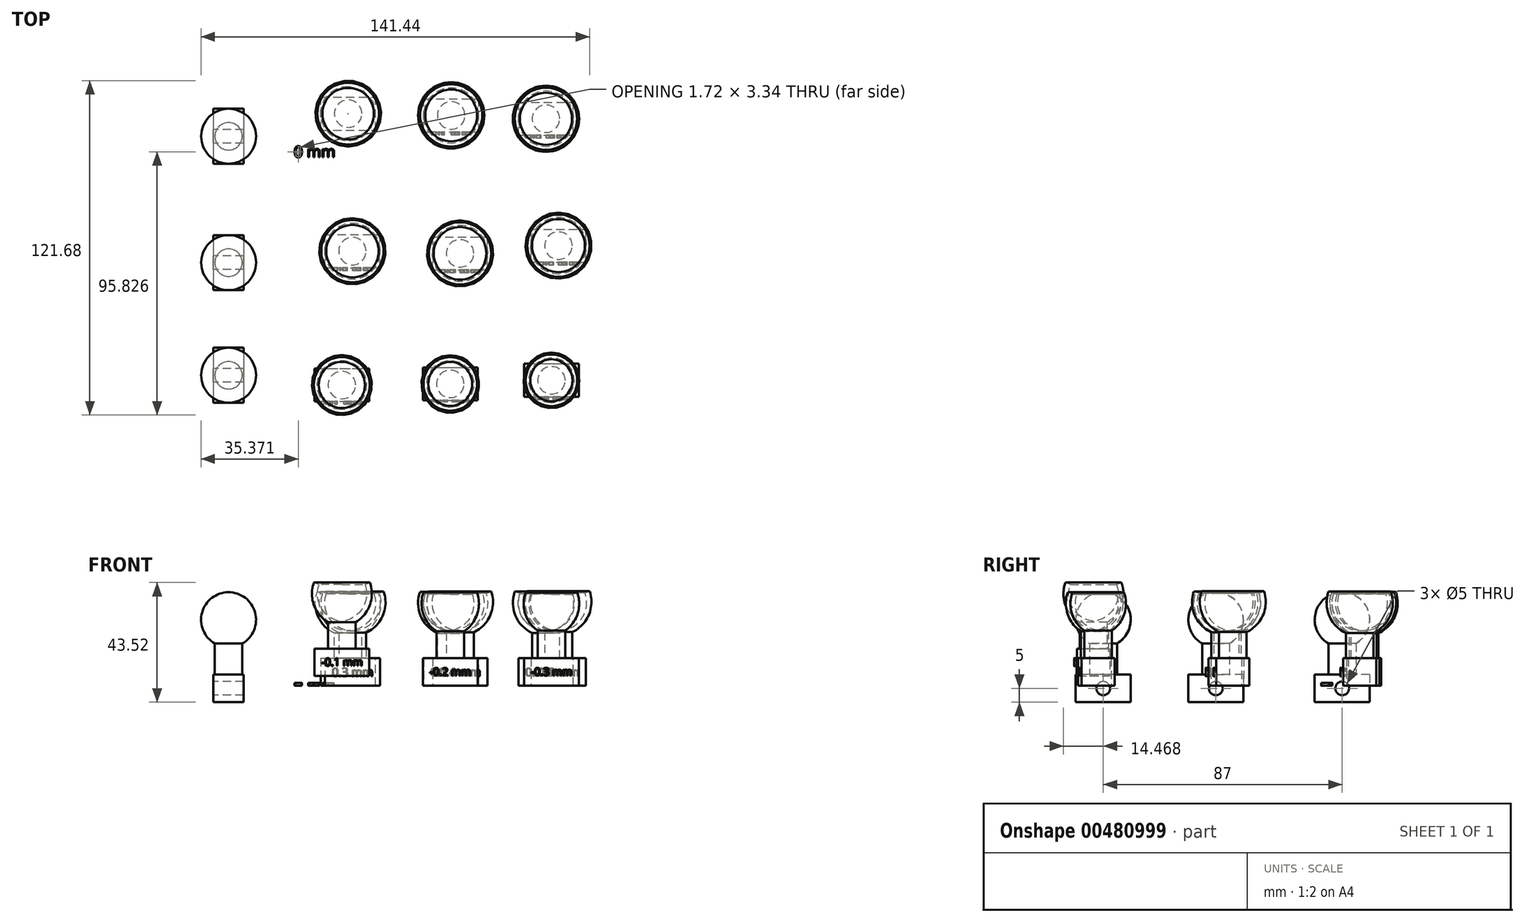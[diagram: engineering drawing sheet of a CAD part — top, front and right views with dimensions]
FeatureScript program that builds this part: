
annotation { "Feature Type Name" : "Feature", "Feature Type Description" : "" }
export const myFeature = defineFeature(function(context is Context, id is Id, definition is map)
    precondition{}
    {
        {
            var Q0;
            Q0=qCreatedBy(makeId("Top.planeOp"),FACE);
            var sketch = newSketch(context, id + "F0", { "sketchPlane" : qUnion([Q0])});
            skLineSegment(sketch, "E0", {"start": v(-54.8, 58.63) * mm, "end": v(-54.8, 38.63) * mm});
            skLineSegment(sketch, "E1", {"start": v(-54.8, 58.63) * mm, "end": v(-64.8, 58.63) * mm});
            skLineSegment(sketch, "E2", {"start": v(-64.8, 58.63) * mm, "end": v(-64.8, 38.63) * mm});
            skLineSegment(sketch, "E3", {"start": v(-64.8, 38.63) * mm, "end": v(-54.8, 38.63) * mm});
            skLineSegment(sketch, "E4", {"start": v(-54.8, 53.63) * mm, "end": v(-43.46, 53.63) * mm});
            skLineSegment(sketch, "E5", {"start": v(-44.8, 48.63) * mm, "end": v(-24.8, 48.63) * mm});
            skArc(sketch, "E6", {"start": v(-24.8, 48.63) * mm, "mid": v(-34.8, 58.63) * mm, "end": v(-44.8, 48.63) * mm});
            skLineSegment(sketch, "E7", {"start": v(-44.8, 48.63) * mm, "end": v(-54.8, 48.63) * mm});
            skSolve(sketch);
        }
        {
            var Q0;
            {var subQ0=sQuery(id+"F0.wireOp",EDGE,"E4");Q0=makeQuery(id+"F0.imprint","IMPRINT",FACE,{"disambiguationData":[TD([[makeQuery(id+"F0.imprint","IMPRINT",EDGE,{"derivedFrom":subQ0}),-1.0]])]});}
            var Q1;
            {var subQ0=sQuery(id+"F0.wireOp",EDGE,"E5");Q1=makeQuery(id+"F0.imprint","IMPRINT",FACE,{"disambiguationData":[TD([[makeQuery(id+"F0.imprint","IMPRINT",EDGE,{"derivedFrom":subQ0}),1.0]])]});}
            var Q2;
            Q2=sQuery(id+"F0.wireOp",EDGE,"E5");
            revolve(context, id + "F1", {"entities" : qUnion([Q0, Q1]), "axis" : qUnion([Q2]), "revolveType" : RevolveType.FULL});
        }
        {
            var Q0;
            {var subQ0=sQuery(id+"F0.wireOp",EDGE,"E1");Q0=makeQuery(id+"F0.imprint","IMPRINT",FACE,{"disambiguationData":[TD([[makeQuery(id+"F0.imprint","IMPRINT",EDGE,{"derivedFrom":subQ0}),1.0]])]});}
            extrude(context, id + "F2", {"entities" : qUnion([Q0]), "operationType" : NewBodyOperationType.ADD, "endBound" : BoundingType.SYMMETRIC, "depth" : 11 * mm});
        }
        {
            var Q0;
            Q0=makeQuery(id+"F1.opRevolve","SWEPT_BODY",BODY,{"disambiguationData":[OSD([sQuery(id+"F0.wireOp",EDGE,"E0"),sQuery(id+"F0.wireOp",EDGE,"E4"),sQuery(id+"F0.wireOp",EDGE,"E5"),sQuery(id+"F0.wireOp",EDGE,"E6"),sQuery(id+"F0.wireOp",EDGE,"E7")])]});
            var Q1;
            Q1=sQuery(id+"F0.wireOp",EDGE,"E2");
            transform(context, id + "F3", {"entities" : qUnion([Q0]), "transformType" : TransformType.ROTATION, "transformAxis" : qUnion([Q1]), "angle" : 90 * degree, "makeCopy" : false});
        }
        {
            var Q0;
            Q0=makeQuery(id+"F1.opRevolve","SWEPT_BODY",BODY,{"disambiguationData":[OSD([sQuery(id+"F0.wireOp",EDGE,"E0"),sQuery(id+"F0.wireOp",EDGE,"E4"),sQuery(id+"F0.wireOp",EDGE,"E5"),sQuery(id+"F0.wireOp",EDGE,"E6"),sQuery(id+"F0.wireOp",EDGE,"E7")])]});
            var Q1;
            Q1=makeQuery(id+"F2.opExtrude","CAP_EDGE",EDGE,{"disambiguationData":[OSD([sQuery(id+"F0.wireOp",EDGE,"E0")])],"isStart":false});
            transform(context, id + "F4", {"entities" : qUnion([Q0]), "transformType" : TransformType.TRANSLATION_ENTITY, "oppositeDirectionEntity" : false, "transformLine" : qUnion([Q1]), "makeCopy" : true});
        }
        {
            var Q0;
            Q0=makeQuery(id+"F4.opPattern","COPY",BODY,{"derivedFrom":makeQuery(id+"F1.opRevolve","SWEPT_BODY",BODY,{"disambiguationData":[OSD([sQuery(id+"F0.wireOp",EDGE,"E0"),sQuery(id+"F0.wireOp",EDGE,"E4"),sQuery(id+"F0.wireOp",EDGE,"E5"),sQuery(id+"F0.wireOp",EDGE,"E6"),sQuery(id+"F0.wireOp",EDGE,"E7")])]}),"instanceName":"1"});
            var Q1;
            Q1=makeQuery(id+"F4.opPattern","COPY",EDGE,{"derivedFrom":makeQuery(id+"F2.opExtrude","CAP_EDGE",EDGE,{"disambiguationData":[OSD([sQuery(id+"F0.wireOp",EDGE,"E2")])],"isStart":false}),"instanceName":"1"});
            transform(context, id + "F5", {"entities" : qUnion([Q0]), "transformType" : TransformType.TRANSLATION_ENTITY, "oppositeDirectionEntity" : false, "transformLine" : qUnion([Q1]), "makeCopy" : false});
        }
        {
            var Q0;
            Q0=makeQuery(id+"F4.opPattern","COPY",BODY,{"derivedFrom":makeQuery(id+"F1.opRevolve","SWEPT_BODY",BODY,{"disambiguationData":[OSD([sQuery(id+"F0.wireOp",EDGE,"E0"),sQuery(id+"F0.wireOp",EDGE,"E4"),sQuery(id+"F0.wireOp",EDGE,"E5"),sQuery(id+"F0.wireOp",EDGE,"E6"),sQuery(id+"F0.wireOp",EDGE,"E7")])]}),"instanceName":"1"});
            var Q1;
            Q1=makeQuery(id+"F4.opPattern","COPY",EDGE,{"derivedFrom":makeQuery(id+"F2.opExtrude","CAP_EDGE",EDGE,{"disambiguationData":[OSD([sQuery(id+"F0.wireOp",EDGE,"E2")])],"isStart":false}),"instanceName":"1"});
            transform(context, id + "F6", {"entities" : qUnion([Q0]), "transformType" : TransformType.TRANSLATION_DISTANCE, "transformDirection" : qUnion([Q1]), "distance" : 40 * mm, "makeCopy" : true});
        }
        {
            var Q0;
            Q0=qCreatedBy(makeId("Top.planeOp"),FACE);
            var sketch = newSketch(context, id + "F7", { "sketchPlane" : qUnion([Q0])});
            skLineSegment(sketch, "E8", {"start": v(-31.27, 60.87) * mm, "end": v(-11.27, 60.87) * mm});
            skLineSegment(sketch, "E9", {"start": v(-31.27, 60.87) * mm, "end": v(-31.27, 50.87) * mm});
            skLineSegment(sketch, "E10", {"start": v(-31.27, 50.87) * mm, "end": v(-11.27, 50.87) * mm});
            skLineSegment(sketch, "E11", {"start": v(-11.27, 50.87) * mm, "end": v(-11.27, 60.87) * mm});
            skLineSegment(sketch, "E12", {"start": v(-26.27, 60.87) * mm, "end": v(-26.27, 72.22) * mm});
            skLineSegment(sketch, "E13", {"start": v(-21.27, 70.87) * mm, "end": v(-21.27, 90.87) * mm});
            skArc(sketch, "E14", {"start": v(-21.27, 90.87) * mm, "mid": v(-31.24, 80.87) * mm, "end": v(-21.27, 70.87) * mm});
            skLineSegment(sketch, "E15", {"start": v(-21.27, 70.87) * mm, "end": v(-21.27, 60.87) * mm});
            skArc(sketch, "E16", {"start": v(-21.27, 92.87) * mm, "mid": v(-33.24, 80.87) * mm, "end": v(-21.27, 68.87) * mm});
            skLineSegment(sketch, "E17", {"start": v(-21.27, 90.87) * mm, "end": v(-21.27, 92.87) * mm});
            skLineSegment(sketch, "E18", {"start": v(-21.24, 80.87) * mm, "end": v(-32.51, 84.97) * mm});
            skSolve(sketch);
        }
        {
            var Q0;
            {var subQ5=sQuery(id+"F7.wireOp",EDGE,"vTw5014h-nTbv-hpdb-avoR-3ejkp2Sw56j0");Q0=makeQuery(id+"F7.imprint","IMPRINT",FACE,{"disambiguationData":[TD([[makeQuery(id+"F7.imprint","IMPRINT",EDGE,{"derivedFrom":subQ5}),1.0]])]});}
            var Q1;
            {var subQ0=sQuery(id+"F7.wireOp",EDGE,"E14");var subQ1=sQuery(id+"F7.wireOp",EDGE,"E12");var subQ2=makeQuery(id+"F7.imprint","INTERSECT",VERTEX,{"derivedFrom":[subQ1,subQ0]});Q1=makeQuery(id+"F7.imprint","IMPRINT",FACE,{"disambiguationData":[TD([[makeQuery(id+"F7.imprint","IMPRINT",EDGE,{"disambiguationData":[TD([[subQ2,1.0]])],"derivedFrom":subQ1}),-1.0]])]});}
            var Q2;
            {var subQ0=sQuery(id+"F7.wireOp",EDGE,"E12");var subQ1=sQuery(id+"F7.wireOp",EDGE,"E8");var subQ2=makeQuery(id+"F7.imprint","INTERSECT",VERTEX,{"derivedFrom":[subQ1,subQ0]});Q2=makeQuery(id+"F7.imprint","IMPRINT",FACE,{"disambiguationData":[TD([[makeQuery(id+"F7.imprint","IMPRINT",EDGE,{"disambiguationData":[TD([[subQ2,-1.0]])],"derivedFrom":subQ1}),1.0]])]});}
            var Q3;
            {var subQ0=sQuery(id+"F7.wireOp",EDGE,"E14");var subQ1=sQuery(id+"F7.wireOp",EDGE,"E12");var subQ2=makeQuery(id+"F7.imprint","INTERSECT",VERTEX,{"derivedFrom":[subQ1,subQ0]});Q3=makeQuery(id+"F7.imprint","IMPRINT",FACE,{"disambiguationData":[TD([[makeQuery(id+"F7.imprint","IMPRINT",EDGE,{"disambiguationData":[TD([[subQ2,1.0]])],"derivedFrom":subQ1}),1.0]])]});}
            var Q4;
            Q4=sQuery(id+"F7.wireOp",EDGE,"E15");
            revolve(context, id + "F8", {"entities" : qUnion([Q0, Q1, Q2, Q3]), "axis" : qUnion([Q4]), "revolveType" : RevolveType.FULL});
        }
        {
            var Q0;
            {var subQ0=sQuery(id+"F7.wireOp",EDGE,"E9");Q0=makeQuery(id+"F7.imprint","IMPRINT",FACE,{"disambiguationData":[TD([[makeQuery(id+"F7.imprint","IMPRINT",EDGE,{"derivedFrom":subQ0}),1.0]])]});}
            extrude(context, id + "F9", {"entities" : qUnion([Q0]), "operationType" : NewBodyOperationType.ADD, "endBound" : BoundingType.SYMMETRIC, "depth" : 12 * mm});
        }
        {
            var Q0;
            Q0=makeQuery(id+"F9.opExtrude","CAP_FACE",FACE,{"disambiguationData":[OSD([sQuery(id+"F7.wireOp",EDGE,"E8"),sQuery(id+"F7.wireOp",EDGE,"E9"),sQuery(id+"F7.wireOp",EDGE,"E10"),sQuery(id+"F7.wireOp",EDGE,"E11")])],"isStart":false});
            var sketch = newSketch(context, id + "F10", { "sketchPlane" : qUnion([Q0])});
            skText(sketch, "E19", { "text": "0 mm", "fontName": "OpenSans-Regular.ttf"});
            const initialGuessF10  = {"E19": [-0.04103, 0.04098, 1, 0, 0.00404]};
            skSetInitialGuess(sketch, initialGuessF10);
            skSolve(sketch);
        }
        {
            var Q0;
            Q0 = qSketchRegion(id + "F10", true);
            extrude(context, id + "F11", {"entities" : qUnion([Q0]), "operationType" : NewBodyOperationType.ADD, "depth" : 1 * mm});
        }
        {
            var Q0;
            Q0=qCreatedBy(makeId("Top.planeOp"),FACE);
            var sketch = newSketch(context, id + "F12", { "sketchPlane" : qUnion([Q0])});
            skLineSegment(sketch, "E20", {"start": v(6.24, 60.21) * mm, "end": v(26.24, 60.21) * mm});
            skLineSegment(sketch, "E21", {"start": v(6.24, 60.21) * mm, "end": v(6.24, 50.21) * mm});
            skLineSegment(sketch, "E22", {"start": v(6.24, 50.21) * mm, "end": v(26.24, 50.21) * mm});
            skLineSegment(sketch, "E23", {"start": v(26.24, 50.21) * mm, "end": v(26.24, 60.21) * mm});
            skLineSegment(sketch, "E24", {"start": v(11.24, 60.21) * mm, "end": v(11.24, 71.54) * mm});
            skLineSegment(sketch, "E25", {"start": v(16.24, 70.21) * mm, "end": v(16.24, 90.31) * mm});
            skArc(sketch, "E26", {"start": v(16.24, 90.31) * mm, "mid": v(6.19, 80.26) * mm, "end": v(16.24, 70.21) * mm});
            skLineSegment(sketch, "E27", {"start": v(16.24, 70.21) * mm, "end": v(16.24, 60.21) * mm});
            skArc(sketch, "E28", {"start": v(16.24, 92.31) * mm, "mid": v(4.19, 80.26) * mm, "end": v(16.24, 68.21) * mm});
            skLineSegment(sketch, "E29", {"start": v(16.24, 90.31) * mm, "end": v(16.24, 92.31) * mm});
            skLineSegment(sketch, "E30", {"start": v(16.24, 80.26) * mm, "end": v(4.91, 84.38) * mm});
            skSolve(sketch);
        }
        {
            var Q0;
            {var subQ0=sQuery(id+"F12.wireOp",EDGE,"E26");var subQ1=sQuery(id+"F12.wireOp",EDGE,"E24");var subQ2=makeQuery(id+"F12.imprint","INTERSECT",VERTEX,{"derivedFrom":[subQ1,subQ0]});Q0=makeQuery(id+"F12.imprint","IMPRINT",FACE,{"disambiguationData":[TD([[makeQuery(id+"F12.imprint","IMPRINT",EDGE,{"disambiguationData":[TD([[subQ2,1.0]])],"derivedFrom":subQ1}),1.0]])]});}
            var Q1;
            {var subQ0=sQuery(id+"F12.wireOp",EDGE,"E26");var subQ1=sQuery(id+"F12.wireOp",EDGE,"E24");var subQ2=makeQuery(id+"F12.imprint","INTERSECT",VERTEX,{"derivedFrom":[subQ1,subQ0]});Q1=makeQuery(id+"F12.imprint","IMPRINT",FACE,{"disambiguationData":[TD([[makeQuery(id+"F12.imprint","IMPRINT",EDGE,{"disambiguationData":[TD([[subQ2,1.0]])],"derivedFrom":subQ1}),-1.0]])]});}
            var Q2;
            {var subQ0=sQuery(id+"F12.wireOp",EDGE,"E24");var subQ1=sQuery(id+"F12.wireOp",EDGE,"E20");var subQ2=makeQuery(id+"F12.imprint","INTERSECT",VERTEX,{"derivedFrom":[subQ1,subQ0]});Q2=makeQuery(id+"F12.imprint","IMPRINT",FACE,{"disambiguationData":[TD([[makeQuery(id+"F12.imprint","IMPRINT",EDGE,{"disambiguationData":[TD([[subQ2,-1.0]])],"derivedFrom":subQ1}),1.0]])]});}
            var Q3;
            Q3=sQuery(id+"F12.wireOp",EDGE,"E27");
            revolve(context, id + "F13", {"entities" : qUnion([Q0, Q1, Q2]), "axis" : qUnion([Q3]), "revolveType" : RevolveType.FULL});
        }
        {
            var Q0;
            {var subQ0=sQuery(id+"F12.wireOp",EDGE,"E21");Q0=makeQuery(id+"F12.imprint","IMPRINT",FACE,{"disambiguationData":[TD([[makeQuery(id+"F12.imprint","IMPRINT",EDGE,{"derivedFrom":subQ0}),1.0]])]});}
            extrude(context, id + "F14", {"entities" : qUnion([Q0]), "operationType" : NewBodyOperationType.ADD, "endBound" : BoundingType.SYMMETRIC, "depth" : 12 * mm});
        }
        {
            var Q0;
            Q0=makeQuery(id+"F14.opExtrude","CAP_FACE",FACE,{"disambiguationData":[OSD([sQuery(id+"F12.wireOp",EDGE,"E20"),sQuery(id+"F12.wireOp",EDGE,"E21"),sQuery(id+"F12.wireOp",EDGE,"E22"),sQuery(id+"F12.wireOp",EDGE,"E23")])],"isStart":false});
            var sketch = newSketch(context, id + "F15", { "sketchPlane" : qUnion([Q0])});
            skText(sketch, "E31", { "text": "0.1 mm", "fontName": "OpenSans-Regular.ttf"});
            const initialGuessF15  = {"E31": [0.00874, 0.05364, 1, 0, 0.00307]};
            skSetInitialGuess(sketch, initialGuessF15);
            skSolve(sketch);
        }
        {
            var Q0;
            Q0 = qSketchRegion(id + "F15", true);
            extrude(context, id + "F16", {"entities" : qUnion([Q0]), "operationType" : NewBodyOperationType.ADD, "depth" : 1 * mm});
        }
        {
            var Q0;
            Q0=qCreatedBy(makeId("Top.planeOp"),FACE);
            var sketch = newSketch(context, id + "F17", { "sketchPlane" : qUnion([Q0])});
            skLineSegment(sketch, "E32", {"start": v(40.75, 59) * mm, "end": v(60.75, 59) * mm});
            skLineSegment(sketch, "E33", {"start": v(40.75, 59) * mm, "end": v(40.75, 49) * mm});
            skLineSegment(sketch, "E34", {"start": v(40.75, 49) * mm, "end": v(60.75, 49) * mm});
            skLineSegment(sketch, "E35", {"start": v(60.75, 49) * mm, "end": v(60.75, 59) * mm});
            skLineSegment(sketch, "E36", {"start": v(45.75, 59) * mm, "end": v(45.75, 70.32) * mm});
            skLineSegment(sketch, "E37", {"start": v(50.75, 69) * mm, "end": v(50.75, 89.2) * mm});
            skArc(sketch, "E38", {"start": v(50.75, 89.2) * mm, "mid": v(40.65, 79.1) * mm, "end": v(50.75, 69) * mm});
            skLineSegment(sketch, "E39", {"start": v(50.75, 69) * mm, "end": v(50.75, 59) * mm});
            skArc(sketch, "E40", {"start": v(50.75, 91.2) * mm, "mid": v(38.7, 79.15) * mm, "end": v(50.75, 67.1) * mm});
            skLineSegment(sketch, "E41", {"start": v(50.75, 89.2) * mm, "end": v(50.75, 91.2) * mm});
            skLineSegment(sketch, "E42", {"start": v(50.75, 79.1) * mm, "end": v(39.4, 83.23) * mm});
            skSolve(sketch);
        }
        {
            var Q0;
            {var subQ0=sQuery(id+"F17.wireOp",EDGE,"E38");var subQ1=sQuery(id+"F17.wireOp",EDGE,"E36");var subQ2=makeQuery(id+"F17.imprint","INTERSECT",VERTEX,{"derivedFrom":[subQ1,subQ0]});Q0=makeQuery(id+"F17.imprint","IMPRINT",FACE,{"disambiguationData":[TD([[makeQuery(id+"F17.imprint","IMPRINT",EDGE,{"disambiguationData":[TD([[subQ2,1.0]])],"derivedFrom":subQ1}),1.0]])]});}
            var Q1;
            {var subQ0=sQuery(id+"F17.wireOp",EDGE,"E38");var subQ1=sQuery(id+"F17.wireOp",EDGE,"E36");var subQ2=makeQuery(id+"F17.imprint","INTERSECT",VERTEX,{"derivedFrom":[subQ1,subQ0]});Q1=makeQuery(id+"F17.imprint","IMPRINT",FACE,{"disambiguationData":[TD([[makeQuery(id+"F17.imprint","IMPRINT",EDGE,{"disambiguationData":[TD([[subQ2,1.0]])],"derivedFrom":subQ1}),-1.0]])]});}
            var Q2;
            {var subQ0=sQuery(id+"F17.wireOp",EDGE,"E36");var subQ1=sQuery(id+"F17.wireOp",EDGE,"E32");var subQ2=makeQuery(id+"F17.imprint","INTERSECT",VERTEX,{"derivedFrom":[subQ1,subQ0]});Q2=makeQuery(id+"F17.imprint","IMPRINT",FACE,{"disambiguationData":[TD([[makeQuery(id+"F17.imprint","IMPRINT",EDGE,{"disambiguationData":[TD([[subQ2,-1.0]])],"derivedFrom":subQ1}),1.0]])]});}
            var Q3;
            Q3=sQuery(id+"F17.wireOp",EDGE,"E39");
            revolve(context, id + "F18", {"entities" : qUnion([Q0, Q1, Q2]), "axis" : qUnion([Q3]), "revolveType" : RevolveType.FULL});
        }
        {
            var Q0;
            {var subQ0=sQuery(id+"F17.wireOp",EDGE,"E33");Q0=makeQuery(id+"F17.imprint","IMPRINT",FACE,{"disambiguationData":[TD([[makeQuery(id+"F17.imprint","IMPRINT",EDGE,{"derivedFrom":subQ0}),1.0]])]});}
            extrude(context, id + "F19", {"entities" : qUnion([Q0]), "operationType" : NewBodyOperationType.ADD, "endBound" : BoundingType.SYMMETRIC, "depth" : 12 * mm});
        }
        {
            var Q0;
            Q0=makeQuery(id+"F19.opExtrude","CAP_FACE",FACE,{"disambiguationData":[OSD([sQuery(id+"F17.wireOp",EDGE,"E32"),sQuery(id+"F17.wireOp",EDGE,"E33"),sQuery(id+"F17.wireOp",EDGE,"E34"),sQuery(id+"F17.wireOp",EDGE,"E35")])],"isStart":false});
            var sketch = newSketch(context, id + "F20", { "sketchPlane" : qUnion([Q0])});
            skText(sketch, "E43", { "text": "0.2 mm", "fontName": "OpenSans-Regular.ttf"});
            const initialGuessF20  = {"E43": [0.04325, 0.05243, 1, 0, 0.00307]};
            skSetInitialGuess(sketch, initialGuessF20);
            skSolve(sketch);
        }
        {
            var Q0;
            Q0 = qSketchRegion(id + "F20", true);
            extrude(context, id + "F21", {"entities" : qUnion([Q0]), "operationType" : NewBodyOperationType.ADD, "depth" : 1 * mm});
        }
        {
            var Q0;
            Q0=qCreatedBy(makeId("Top.planeOp"),FACE);
            var sketch = newSketch(context, id + "F22", { "sketchPlane" : qUnion([Q0])});
            skLineSegment(sketch, "E44", {"start": v(-29.71, 10.81) * mm, "end": v(-9.71, 10.81) * mm});
            skLineSegment(sketch, "E45", {"start": v(-29.71, 10.81) * mm, "end": v(-29.71, 0.81) * mm});
            skLineSegment(sketch, "E46", {"start": v(-29.71, 0.81) * mm, "end": v(-9.71, 0.81) * mm});
            skLineSegment(sketch, "E47", {"start": v(-9.71, 0.81) * mm, "end": v(-9.71, 10.81) * mm});
            skLineSegment(sketch, "E48", {"start": v(-24.71, 10.81) * mm, "end": v(-24.71, 22.13) * mm});
            skLineSegment(sketch, "E49", {"start": v(-19.71, 20.81) * mm, "end": v(-19.71, 41.11) * mm});
            skArc(sketch, "E50", {"start": v(-19.71, 41.11) * mm, "mid": v(-29.86, 30.96) * mm, "end": v(-19.71, 20.81) * mm});
            skLineSegment(sketch, "E51", {"start": v(-19.71, 20.81) * mm, "end": v(-19.71, 10.81) * mm});
            skArc(sketch, "E52", {"start": v(-19.71, 43.11) * mm, "mid": v(-31.74, 31.06) * mm, "end": v(-19.71, 19.01) * mm});
            skLineSegment(sketch, "E53", {"start": v(-19.71, 41.11) * mm, "end": v(-19.71, 43.11) * mm});
            skLineSegment(sketch, "E54", {"start": v(-19.71, 30.96) * mm, "end": v(-31.05, 35.09) * mm});
            skSolve(sketch);
        }
        {
            var Q0;
            {var subQ0=sQuery(id+"F22.wireOp",EDGE,"E50");var subQ1=sQuery(id+"F22.wireOp",EDGE,"E48");var subQ2=makeQuery(id+"F22.imprint","INTERSECT",VERTEX,{"derivedFrom":[subQ1,subQ0]});Q0=makeQuery(id+"F22.imprint","IMPRINT",FACE,{"disambiguationData":[TD([[makeQuery(id+"F22.imprint","IMPRINT",EDGE,{"disambiguationData":[TD([[subQ2,1.0]])],"derivedFrom":subQ1}),1.0]])]});}
            var Q1;
            {var subQ0=sQuery(id+"F22.wireOp",EDGE,"E50");var subQ1=sQuery(id+"F22.wireOp",EDGE,"E48");var subQ2=makeQuery(id+"F22.imprint","INTERSECT",VERTEX,{"derivedFrom":[subQ1,subQ0]});Q1=makeQuery(id+"F22.imprint","IMPRINT",FACE,{"disambiguationData":[TD([[makeQuery(id+"F22.imprint","IMPRINT",EDGE,{"disambiguationData":[TD([[subQ2,1.0]])],"derivedFrom":subQ1}),-1.0]])]});}
            var Q2;
            {var subQ0=sQuery(id+"F22.wireOp",EDGE,"E48");var subQ1=sQuery(id+"F22.wireOp",EDGE,"E44");var subQ2=makeQuery(id+"F22.imprint","INTERSECT",VERTEX,{"derivedFrom":[subQ1,subQ0]});Q2=makeQuery(id+"F22.imprint","IMPRINT",FACE,{"disambiguationData":[TD([[makeQuery(id+"F22.imprint","IMPRINT",EDGE,{"disambiguationData":[TD([[subQ2,-1.0]])],"derivedFrom":subQ1}),1.0]])]});}
            var Q3;
            Q3=sQuery(id+"F22.wireOp",EDGE,"E49");
            revolve(context, id + "F23", {"entities" : qUnion([Q0, Q1, Q2]), "axis" : qUnion([Q3]), "revolveType" : RevolveType.FULL});
        }
        {
            var Q0;
            {var subQ0=sQuery(id+"F22.wireOp",EDGE,"E45");Q0=makeQuery(id+"F22.imprint","IMPRINT",FACE,{"disambiguationData":[TD([[makeQuery(id+"F22.imprint","IMPRINT",EDGE,{"derivedFrom":subQ0}),1.0]])]});}
            extrude(context, id + "F24", {"entities" : qUnion([Q0]), "operationType" : NewBodyOperationType.ADD, "endBound" : BoundingType.SYMMETRIC, "depth" : 12 * mm});
        }
        {
            var Q0;
            Q0=qCreatedBy(makeId("Top.planeOp"),FACE);
            var sketch = newSketch(context, id + "F25", { "sketchPlane" : qUnion([Q0])});
            skLineSegment(sketch, "E55", {"start": v(9.45, 10) * mm, "end": v(29.45, 10) * mm});
            skLineSegment(sketch, "E56", {"start": v(9.45, 10) * mm, "end": v(9.45, 0) * mm});
            skLineSegment(sketch, "E57", {"start": v(9.45, 0) * mm, "end": v(29.45, 0) * mm});
            skLineSegment(sketch, "E58", {"start": v(29.45, 0) * mm, "end": v(29.45, 10) * mm});
            skLineSegment(sketch, "E59", {"start": v(14.45, 10) * mm, "end": v(14.45, 21.3) * mm});
            skLineSegment(sketch, "E60", {"start": v(19.45, 20) * mm, "end": v(19.45, 40.4) * mm});
            skArc(sketch, "E61", {"start": v(19.45, 40.4) * mm, "mid": v(9.25, 30.2) * mm, "end": v(19.45, 20) * mm});
            skLineSegment(sketch, "E62", {"start": v(19.45, 20) * mm, "end": v(19.45, 10) * mm});
            skArc(sketch, "E63", {"start": v(19.45, 42.4) * mm, "mid": v(7.44, 30.35) * mm, "end": v(19.45, 18.3) * mm});
            skLineSegment(sketch, "E64", {"start": v(19.45, 40.4) * mm, "end": v(19.45, 42.4) * mm});
            skLineSegment(sketch, "E65", {"start": v(19.45, 30.2) * mm, "end": v(8.11, 34.33) * mm});
            skSolve(sketch);
        }
        {
            var Q0;
            {var subQ0=sQuery(id+"F25.wireOp",EDGE,"E59");var subQ1=sQuery(id+"F25.wireOp",EDGE,"E55");var subQ2=makeQuery(id+"F25.imprint","INTERSECT",VERTEX,{"derivedFrom":[subQ1,subQ0]});Q0=makeQuery(id+"F25.imprint","IMPRINT",FACE,{"disambiguationData":[TD([[makeQuery(id+"F25.imprint","IMPRINT",EDGE,{"disambiguationData":[TD([[subQ2,-1.0]])],"derivedFrom":subQ1}),1.0]])]});}
            var Q1;
            {var subQ0=sQuery(id+"F25.wireOp",EDGE,"E61");var subQ1=sQuery(id+"F25.wireOp",EDGE,"E59");var subQ2=makeQuery(id+"F25.imprint","INTERSECT",VERTEX,{"derivedFrom":[subQ1,subQ0]});Q1=makeQuery(id+"F25.imprint","IMPRINT",FACE,{"disambiguationData":[TD([[makeQuery(id+"F25.imprint","IMPRINT",EDGE,{"disambiguationData":[TD([[subQ2,1.0]])],"derivedFrom":subQ1}),-1.0]])]});}
            var Q2;
            {var subQ0=sQuery(id+"F25.wireOp",EDGE,"E61");var subQ1=sQuery(id+"F25.wireOp",EDGE,"E59");var subQ2=makeQuery(id+"F25.imprint","INTERSECT",VERTEX,{"derivedFrom":[subQ1,subQ0]});Q2=makeQuery(id+"F25.imprint","IMPRINT",FACE,{"disambiguationData":[TD([[makeQuery(id+"F25.imprint","IMPRINT",EDGE,{"disambiguationData":[TD([[subQ2,1.0]])],"derivedFrom":subQ1}),1.0]])]});}
            var Q3;
            Q3=sQuery(id+"F25.wireOp",EDGE,"E60");
            revolve(context, id + "F26", {"entities" : qUnion([Q0, Q1, Q2]), "axis" : qUnion([Q3]), "revolveType" : RevolveType.FULL});
        }
        {
            var Q0;
            {var subQ0=sQuery(id+"F25.wireOp",EDGE,"E56");Q0=makeQuery(id+"F25.imprint","IMPRINT",FACE,{"disambiguationData":[TD([[makeQuery(id+"F25.imprint","IMPRINT",EDGE,{"derivedFrom":subQ0}),1.0]])]});}
            extrude(context, id + "F27", {"entities" : qUnion([Q0]), "operationType" : NewBodyOperationType.ADD, "endBound" : BoundingType.SYMMETRIC, "depth" : 12 * mm});
        }
        {
            var Q0;
            Q0=qCreatedBy(makeId("Top.planeOp"),FACE);
            var sketch = newSketch(context, id + "F28", { "sketchPlane" : qUnion([Q0])});
            skLineSegment(sketch, "E66", {"start": v(45.3, 12.8) * mm, "end": v(65.3, 12.8) * mm});
            skLineSegment(sketch, "E67", {"start": v(45.3, 12.8) * mm, "end": v(45.3, 2.8) * mm});
            skLineSegment(sketch, "E68", {"start": v(45.3, 2.8) * mm, "end": v(65.3, 2.8) * mm});
            skLineSegment(sketch, "E69", {"start": v(65.3, 2.8) * mm, "end": v(65.3, 12.8) * mm});
            skLineSegment(sketch, "E70", {"start": v(50.3, 12.8) * mm, "end": v(50.3, 24.1) * mm});
            skLineSegment(sketch, "E71", {"start": v(55.3, 22.8) * mm, "end": v(55.3, 43.3) * mm});
            skArc(sketch, "E72", {"start": v(55.3, 43.3) * mm, "mid": v(45.05, 33.05) * mm, "end": v(55.3, 22.8) * mm});
            skLineSegment(sketch, "E73", {"start": v(55.3, 22.8) * mm, "end": v(55.3, 12.8) * mm});
            skArc(sketch, "E74", {"start": v(55.3, 45.3) * mm, "mid": v(43.3, 33.25) * mm, "end": v(55.3, 21.2) * mm});
            skLineSegment(sketch, "E75", {"start": v(55.3, 43.3) * mm, "end": v(55.3, 45.3) * mm});
            skLineSegment(sketch, "E76", {"start": v(55.3, 33.05) * mm, "end": v(43.96, 37.18) * mm});
            skSolve(sketch);
        }
        {
            var Q0;
            {var subQ0=sQuery(id+"F28.wireOp",EDGE,"E72");var subQ1=sQuery(id+"F28.wireOp",EDGE,"E70");var subQ2=makeQuery(id+"F28.imprint","INTERSECT",VERTEX,{"derivedFrom":[subQ1,subQ0]});Q0=makeQuery(id+"F28.imprint","IMPRINT",FACE,{"disambiguationData":[TD([[makeQuery(id+"F28.imprint","IMPRINT",EDGE,{"disambiguationData":[TD([[subQ2,1.0]])],"derivedFrom":subQ1}),1.0]])]});}
            var Q1;
            {var subQ0=sQuery(id+"F28.wireOp",EDGE,"E72");var subQ1=sQuery(id+"F28.wireOp",EDGE,"E70");var subQ2=makeQuery(id+"F28.imprint","INTERSECT",VERTEX,{"derivedFrom":[subQ1,subQ0]});Q1=makeQuery(id+"F28.imprint","IMPRINT",FACE,{"disambiguationData":[TD([[makeQuery(id+"F28.imprint","IMPRINT",EDGE,{"disambiguationData":[TD([[subQ2,1.0]])],"derivedFrom":subQ1}),-1.0]])]});}
            var Q2;
            {var subQ0=sQuery(id+"F28.wireOp",EDGE,"E70");var subQ1=sQuery(id+"F28.wireOp",EDGE,"E66");var subQ2=makeQuery(id+"F28.imprint","INTERSECT",VERTEX,{"derivedFrom":[subQ1,subQ0]});Q2=makeQuery(id+"F28.imprint","IMPRINT",FACE,{"disambiguationData":[TD([[makeQuery(id+"F28.imprint","IMPRINT",EDGE,{"disambiguationData":[TD([[subQ2,-1.0]])],"derivedFrom":subQ1}),1.0]])]});}
            var Q3;
            Q3=sQuery(id+"F28.wireOp",EDGE,"E71");
            revolve(context, id + "F29", {"entities" : qUnion([Q0, Q1, Q2]), "axis" : qUnion([Q3]), "revolveType" : RevolveType.FULL});
        }
        {
            var Q0;
            {var subQ0=sQuery(id+"F28.wireOp",EDGE,"E67");Q0=makeQuery(id+"F28.imprint","IMPRINT",FACE,{"disambiguationData":[TD([[makeQuery(id+"F28.imprint","IMPRINT",EDGE,{"derivedFrom":subQ0}),1.0]])]});}
            extrude(context, id + "F30", {"entities" : qUnion([Q0]), "operationType" : NewBodyOperationType.ADD, "endBound" : BoundingType.SYMMETRIC, "depth" : 12 * mm});
        }
        {
            var Q0;
            Q0=qCreatedBy(makeId("Top.planeOp"),FACE);
            var sketch = newSketch(context, id + "F31", { "sketchPlane" : qUnion([Q0])});
            skLineSegment(sketch, "E77", {"start": v(-33.57, -37.93) * mm, "end": v(-13.57, -37.93) * mm});
            skLineSegment(sketch, "E78", {"start": v(-33.57, -37.93) * mm, "end": v(-33.57, -47.93) * mm});
            skLineSegment(sketch, "E79", {"start": v(-33.57, -47.93) * mm, "end": v(-13.57, -47.93) * mm});
            skLineSegment(sketch, "E80", {"start": v(-13.57, -47.93) * mm, "end": v(-13.57, -37.93) * mm});
            skLineSegment(sketch, "E81", {"start": v(-28.57, -37.93) * mm, "end": v(-28.57, -25.98) * mm});
            skLineSegment(sketch, "E82", {"start": v(-23.57, -27.93) * mm, "end": v(-23.57, -8.03) * mm});
            skArc(sketch, "E83", {"start": v(-23.57, -8.03) * mm, "mid": v(-32.57, -17.98) * mm, "end": v(-23.57, -27.93) * mm});
            skLineSegment(sketch, "E84", {"start": v(-23.57, -27.93) * mm, "end": v(-23.57, -37.93) * mm});
            skArc(sketch, "E85", {"start": v(-23.57, -6.03) * mm, "mid": v(-34.47, -17.98) * mm, "end": v(-23.57, -29.93) * mm});
            skLineSegment(sketch, "E86", {"start": v(-23.57, -8.03) * mm, "end": v(-23.57, -6.03) * mm});
            skLineSegment(sketch, "E87", {"start": v(-22.57, -17.98) * mm, "end": v(-33.76, -13.9) * mm});
            skSolve(sketch);
        }
        {
            var Q0;
            {var subQ0=sQuery(id+"F31.wireOp",EDGE,"E83");var subQ1=sQuery(id+"F31.wireOp",EDGE,"E81");var subQ2=makeQuery(id+"F31.imprint","INTERSECT",VERTEX,{"derivedFrom":[subQ1,subQ0]});Q0=makeQuery(id+"F31.imprint","IMPRINT",FACE,{"disambiguationData":[TD([[makeQuery(id+"F31.imprint","IMPRINT",EDGE,{"disambiguationData":[TD([[subQ2,1.0]])],"derivedFrom":subQ1}),1.0]])]});}
            var Q1;
            {var subQ0=sQuery(id+"F31.wireOp",EDGE,"E83");var subQ1=sQuery(id+"F31.wireOp",EDGE,"E81");var subQ2=makeQuery(id+"F31.imprint","INTERSECT",VERTEX,{"derivedFrom":[subQ1,subQ0]});Q1=makeQuery(id+"F31.imprint","IMPRINT",FACE,{"disambiguationData":[TD([[makeQuery(id+"F31.imprint","IMPRINT",EDGE,{"disambiguationData":[TD([[subQ2,1.0]])],"derivedFrom":subQ1}),-1.0]])]});}
            var Q2;
            {var subQ0=sQuery(id+"F31.wireOp",EDGE,"E81");var subQ1=sQuery(id+"F31.wireOp",EDGE,"E77");var subQ2=makeQuery(id+"F31.imprint","INTERSECT",VERTEX,{"derivedFrom":[subQ1,subQ0]});Q2=makeQuery(id+"F31.imprint","IMPRINT",FACE,{"disambiguationData":[TD([[makeQuery(id+"F31.imprint","IMPRINT",EDGE,{"disambiguationData":[TD([[subQ2,-1.0]])],"derivedFrom":subQ1}),1.0]])]});}
            var Q3;
            Q3=sQuery(id+"F31.wireOp",EDGE,"E82");
            revolve(context, id + "F32", {"entities" : qUnion([Q0, Q1, Q2]), "axis" : qUnion([Q3]), "revolveType" : RevolveType.FULL});
        }
        {
            var Q0;
            {var subQ0=sQuery(id+"F31.wireOp",EDGE,"E78");Q0=makeQuery(id+"F31.imprint","IMPRINT",FACE,{"disambiguationData":[TD([[makeQuery(id+"F31.imprint","IMPRINT",EDGE,{"derivedFrom":subQ0}),1.0]])]});}
            extrude(context, id + "F33", {"entities" : qUnion([Q0]), "operationType" : NewBodyOperationType.ADD, "endBound" : BoundingType.SYMMETRIC, "depth" : 12 * mm});
        }
        {
            var Q0;
            Q0=qCreatedBy(makeId("Top.planeOp"),FACE);
            var sketch = newSketch(context, id + "F34", { "sketchPlane" : qUnion([Q0])});
            skLineSegment(sketch, "E88", {"start": v(5.9, -37.53) * mm, "end": v(25.9, -37.53) * mm});
            skLineSegment(sketch, "E89", {"start": v(5.9, -37.53) * mm, "end": v(5.9, -47.53) * mm});
            skLineSegment(sketch, "E90", {"start": v(5.9, -47.53) * mm, "end": v(25.9, -47.53) * mm});
            skLineSegment(sketch, "E91", {"start": v(25.9, -47.53) * mm, "end": v(25.9, -37.53) * mm});
            skLineSegment(sketch, "E92", {"start": v(10.9, -37.53) * mm, "end": v(10.9, -25.3) * mm});
            skLineSegment(sketch, "E93", {"start": v(15.9, -27.53) * mm, "end": v(15.9, -7.73) * mm});
            skArc(sketch, "E94", {"start": v(15.9, -7.73) * mm, "mid": v(7.31, -17.63) * mm, "end": v(15.9, -27.53) * mm});
            skLineSegment(sketch, "E95", {"start": v(15.9, -27.53) * mm, "end": v(15.9, -37.53) * mm});
            skArc(sketch, "E96", {"start": v(15.9, -5.73) * mm, "mid": v(5.45, -17.63) * mm, "end": v(15.9, -29.53) * mm});
            skLineSegment(sketch, "E97", {"start": v(15.9, -7.73) * mm, "end": v(15.9, -5.73) * mm});
            skLineSegment(sketch, "E98", {"start": v(17.31, -17.63) * mm, "end": v(6.15, -13.57) * mm});
            skSolve(sketch);
        }
        {
            var Q0;
            {var subQ0=sQuery(id+"F34.wireOp",EDGE,"E94");var subQ1=sQuery(id+"F34.wireOp",EDGE,"E92");var subQ2=makeQuery(id+"F34.imprint","INTERSECT",VERTEX,{"derivedFrom":[subQ1,subQ0]});Q0=makeQuery(id+"F34.imprint","IMPRINT",FACE,{"disambiguationData":[TD([[makeQuery(id+"F34.imprint","IMPRINT",EDGE,{"disambiguationData":[TD([[subQ2,1.0]])],"derivedFrom":subQ1}),1.0]])]});}
            var Q1;
            {var subQ0=sQuery(id+"F34.wireOp",EDGE,"E94");var subQ1=sQuery(id+"F34.wireOp",EDGE,"E92");var subQ2=makeQuery(id+"F34.imprint","INTERSECT",VERTEX,{"derivedFrom":[subQ1,subQ0]});Q1=makeQuery(id+"F34.imprint","IMPRINT",FACE,{"disambiguationData":[TD([[makeQuery(id+"F34.imprint","IMPRINT",EDGE,{"disambiguationData":[TD([[subQ2,1.0]])],"derivedFrom":subQ1}),-1.0]])]});}
            var Q2;
            {var subQ0=sQuery(id+"F34.wireOp",EDGE,"E92");var subQ1=sQuery(id+"F34.wireOp",EDGE,"E88");var subQ2=makeQuery(id+"F34.imprint","INTERSECT",VERTEX,{"derivedFrom":[subQ1,subQ0]});Q2=makeQuery(id+"F34.imprint","IMPRINT",FACE,{"disambiguationData":[TD([[makeQuery(id+"F34.imprint","IMPRINT",EDGE,{"disambiguationData":[TD([[subQ2,-1.0]])],"derivedFrom":subQ1}),1.0]])]});}
            var Q3;
            Q3=sQuery(id+"F34.wireOp",EDGE,"E93");
            revolve(context, id + "F35", {"entities" : qUnion([Q0, Q1, Q2]), "axis" : qUnion([Q3]), "revolveType" : RevolveType.FULL});
        }
        {
            var Q0;
            {var subQ0=sQuery(id+"F34.wireOp",EDGE,"E89");Q0=makeQuery(id+"F34.imprint","IMPRINT",FACE,{"disambiguationData":[TD([[makeQuery(id+"F34.imprint","IMPRINT",EDGE,{"derivedFrom":subQ0}),1.0]])]});}
            extrude(context, id + "F36", {"entities" : qUnion([Q0]), "operationType" : NewBodyOperationType.ADD, "endBound" : BoundingType.SYMMETRIC, "depth" : 12 * mm});
        }
        {
            var Q0;
            Q0=qCreatedBy(makeId("Top.planeOp"),FACE);
            var sketch = newSketch(context, id + "F37", { "sketchPlane" : qUnion([Q0])});
            skLineSegment(sketch, "E99", {"start": v(42.74, -36.21) * mm, "end": v(62.74, -36.21) * mm});
            skLineSegment(sketch, "E100", {"start": v(42.74, -36.21) * mm, "end": v(42.74, -46.21) * mm});
            skLineSegment(sketch, "E101", {"start": v(42.74, -46.21) * mm, "end": v(62.74, -46.21) * mm});
            skLineSegment(sketch, "E102", {"start": v(62.74, -46.21) * mm, "end": v(62.74, -36.21) * mm});
            skLineSegment(sketch, "E103", {"start": v(47.74, -36.21) * mm, "end": v(47.74, -23.76) * mm});
            skLineSegment(sketch, "E104", {"start": v(52.74, -26.21) * mm, "end": v(52.74, -6.51) * mm});
            skArc(sketch, "E105", {"start": v(52.74, -6.51) * mm, "mid": v(44.47, -16.36) * mm, "end": v(52.74, -26.21) * mm});
            skLineSegment(sketch, "E106", {"start": v(52.74, -26.21) * mm, "end": v(52.74, -36.21) * mm});
            skArc(sketch, "E107", {"start": v(52.74, -4.51) * mm, "mid": v(42.64, -16.36) * mm, "end": v(52.74, -28.21) * mm});
            skLineSegment(sketch, "E108", {"start": v(52.74, -6.51) * mm, "end": v(52.74, -4.51) * mm});
            skLineSegment(sketch, "E109", {"start": v(54.47, -16.36) * mm, "end": v(43.34, -12.31) * mm});
            skSolve(sketch);
        }
        {
            var Q0;
            {var subQ0=sQuery(id+"F37.wireOp",EDGE,"E105");var subQ1=sQuery(id+"F37.wireOp",EDGE,"E103");var subQ2=makeQuery(id+"F37.imprint","INTERSECT",VERTEX,{"derivedFrom":[subQ1,subQ0]});Q0=makeQuery(id+"F37.imprint","IMPRINT",FACE,{"disambiguationData":[TD([[makeQuery(id+"F37.imprint","IMPRINT",EDGE,{"disambiguationData":[TD([[subQ2,1.0]])],"derivedFrom":subQ1}),1.0]])]});}
            var Q1;
            {var subQ0=sQuery(id+"F37.wireOp",EDGE,"E105");var subQ1=sQuery(id+"F37.wireOp",EDGE,"E103");var subQ2=makeQuery(id+"F37.imprint","INTERSECT",VERTEX,{"derivedFrom":[subQ1,subQ0]});Q1=makeQuery(id+"F37.imprint","IMPRINT",FACE,{"disambiguationData":[TD([[makeQuery(id+"F37.imprint","IMPRINT",EDGE,{"disambiguationData":[TD([[subQ2,1.0]])],"derivedFrom":subQ1}),-1.0]])]});}
            var Q2;
            {var subQ0=sQuery(id+"F37.wireOp",EDGE,"E103");var subQ1=sQuery(id+"F37.wireOp",EDGE,"E99");var subQ2=makeQuery(id+"F37.imprint","INTERSECT",VERTEX,{"derivedFrom":[subQ1,subQ0]});Q2=makeQuery(id+"F37.imprint","IMPRINT",FACE,{"disambiguationData":[TD([[makeQuery(id+"F37.imprint","IMPRINT",EDGE,{"disambiguationData":[TD([[subQ2,-1.0]])],"derivedFrom":subQ1}),1.0]])]});}
            var Q3;
            Q3=sQuery(id+"F37.wireOp",EDGE,"E104");
            revolve(context, id + "F38", {"entities" : qUnion([Q0, Q1, Q2]), "axis" : qUnion([Q3]), "revolveType" : RevolveType.FULL});
        }
        {
            var Q0;
            {var subQ0=sQuery(id+"F37.wireOp",EDGE,"E100");Q0=makeQuery(id+"F37.imprint","IMPRINT",FACE,{"disambiguationData":[TD([[makeQuery(id+"F37.imprint","IMPRINT",EDGE,{"derivedFrom":subQ0}),1.0]])]});}
            extrude(context, id + "F39", {"entities" : qUnion([Q0]), "operationType" : NewBodyOperationType.ADD, "endBound" : BoundingType.SYMMETRIC, "depth" : 12 * mm});
        }
        {
            var Q0;
            Q0=makeQuery(id+"F24.opExtrude","CAP_FACE",FACE,{"disambiguationData":[OSD([sQuery(id+"F22.wireOp",EDGE,"E44"),sQuery(id+"F22.wireOp",EDGE,"E45"),sQuery(id+"F22.wireOp",EDGE,"E46"),sQuery(id+"F22.wireOp",EDGE,"E47")])],"isStart":false});
            var sketch = newSketch(context, id + "F40", { "sketchPlane" : qUnion([Q0])});
            skText(sketch, "E110", { "text": "0.3 mm", "fontName": "OpenSans-Regular.ttf"});
            const initialGuessF40  = {"E110": [-0.02721, 0.00424, 1, 0, 0.00307]};
            skSetInitialGuess(sketch, initialGuessF40);
            skSolve(sketch);
        }
        {
            var Q0;
            Q0 = qSketchRegion(id + "F40", true);
            extrude(context, id + "F41", {"entities" : qUnion([Q0]), "operationType" : NewBodyOperationType.ADD, "depth" : 1 * mm});
        }
        {
            var Q0;
            Q0=makeQuery(id+"F27.opExtrude","CAP_FACE",FACE,{"disambiguationData":[OSD([sQuery(id+"F25.wireOp",EDGE,"E55"),sQuery(id+"F25.wireOp",EDGE,"E56"),sQuery(id+"F25.wireOp",EDGE,"E57"),sQuery(id+"F25.wireOp",EDGE,"E58")])],"isStart":false});
            var sketch = newSketch(context, id + "F42", { "sketchPlane" : qUnion([Q0])});
            skText(sketch, "E111", { "text": "0.4 mm", "fontName": "OpenSans-Regular.ttf"});
            const initialGuessF42  = {"E111": [0.01195, 0.00343, 1, 0, 0.00307]};
            skSetInitialGuess(sketch, initialGuessF42);
            skSolve(sketch);
        }
        {
            var Q0;
            Q0 = qSketchRegion(id + "F42", true);
            extrude(context, id + "F43", {"entities" : qUnion([Q0]), "operationType" : NewBodyOperationType.ADD, "depth" : 1 * mm});
        }
        {
            var Q0;
            Q0=makeQuery(id+"F30.opExtrude","CAP_FACE",FACE,{"disambiguationData":[OSD([sQuery(id+"F28.wireOp",EDGE,"E66"),sQuery(id+"F28.wireOp",EDGE,"E67"),sQuery(id+"F28.wireOp",EDGE,"E68"),sQuery(id+"F28.wireOp",EDGE,"E69")])],"isStart":false});
            var sketch = newSketch(context, id + "F44", { "sketchPlane" : qUnion([Q0])});
            skText(sketch, "E112", { "text": "0.5 mm", "fontName": "OpenSans-Regular.ttf"});
            const initialGuessF44  = {"E112": [0.0478, 0.00623, 1, 0, 0.00307]};
            skSetInitialGuess(sketch, initialGuessF44);
            skSolve(sketch);
        }
        {
            var Q0;
            Q0 = qSketchRegion(id + "F44", true);
            extrude(context, id + "F45", {"entities" : qUnion([Q0]), "operationType" : NewBodyOperationType.ADD, "depth" : 1 * mm});
        }
        {
            var Q0;
            Q0=makeQuery(id+"F33.opExtrude","CAP_FACE",FACE,{"disambiguationData":[OSD([sQuery(id+"F31.wireOp",EDGE,"E77"),sQuery(id+"F31.wireOp",EDGE,"E78"),sQuery(id+"F31.wireOp",EDGE,"E79"),sQuery(id+"F31.wireOp",EDGE,"E80")])],"isStart":false});
            var sketch = newSketch(context, id + "F46", { "sketchPlane" : qUnion([Q0])});
            skText(sketch, "E113", { "text": "-0.1 mm", "fontName": "OpenSans-Regular.ttf"});
            const initialGuessF46  = {"E113": [-0.03107, -0.04425, 1, 0, 0.00282]};
            skSetInitialGuess(sketch, initialGuessF46);
            skSolve(sketch);
        }
        {
            var Q0;
            Q0 = qSketchRegion(id + "F46", true);
            extrude(context, id + "F47", {"entities" : qUnion([Q0]), "operationType" : NewBodyOperationType.ADD, "depth" : 1 * mm});
        }
        {
            var Q0;
            Q0=makeQuery(id+"F36.opExtrude","CAP_FACE",FACE,{"disambiguationData":[OSD([sQuery(id+"F34.wireOp",EDGE,"E88"),sQuery(id+"F34.wireOp",EDGE,"E89"),sQuery(id+"F34.wireOp",EDGE,"E90"),sQuery(id+"F34.wireOp",EDGE,"E91")])],"isStart":false});
            var sketch = newSketch(context, id + "F48", { "sketchPlane" : qUnion([Q0])});
            skText(sketch, "E114", { "text": "-0.2 mm", "fontName": "OpenSans-Regular.ttf"});
            const initialGuessF48  = {"E114": [0.0084, -0.04384, 1, 0, 0.00282]};
            skSetInitialGuess(sketch, initialGuessF48);
            skSolve(sketch);
        }
        {
            var Q0;
            Q0 = qSketchRegion(id + "F48", true);
            extrude(context, id + "F49", {"entities" : qUnion([Q0]), "operationType" : NewBodyOperationType.ADD, "endBound" : BoundingType.SYMMETRIC, "depth" : 1 * mm});
        }
        {
            var Q0;
            Q0=makeQuery(id+"F39.opExtrude","CAP_FACE",FACE,{"disambiguationData":[OSD([sQuery(id+"F37.wireOp",EDGE,"E99"),sQuery(id+"F37.wireOp",EDGE,"E100"),sQuery(id+"F37.wireOp",EDGE,"E101"),sQuery(id+"F37.wireOp",EDGE,"E102")])],"isStart":false});
            var sketch = newSketch(context, id + "F50", { "sketchPlane" : qUnion([Q0])});
            skText(sketch, "E115", { "text": "-0.3 mm", "fontName": "OpenSans-Regular.ttf"});
            const initialGuessF50  = {"E115": [0.04524, -0.04253, 1, 0, 0.00282]};
            skSetInitialGuess(sketch, initialGuessF50);
            skSolve(sketch);
        }
        {
            var Q0;
            Q0 = qSketchRegion(id + "F50", true);
            extrude(context, id + "F51", {"entities" : qUnion([Q0]), "operationType" : NewBodyOperationType.ADD, "depth" : 1 * mm});
        }
        {
            var Q0;
            Q0=makeQuery(id+"F8.opRevolve","SWEPT_BODY",BODY,{"disambiguationData":[OSD([sQuery(id+"F7.wireOp",EDGE,"E8"),sQuery(id+"F7.wireOp",EDGE,"E12"),sQuery(id+"F7.wireOp",EDGE,"E14"),sQuery(id+"F7.wireOp",EDGE,"E15"),sQuery(id+"F7.wireOp",EDGE,"E16"),sQuery(id+"F7.wireOp",EDGE,"E18")])]});
            var Q1;
            Q1=makeQuery(id+"F9.opExtrude","CAP_EDGE",EDGE,{"disambiguationData":[OSD([sQuery(id+"F7.wireOp",EDGE,"E10")])],"isStart":false});
            var Q2;
            Q2=makeQuery(id+"F9.opExtrude","CAP_EDGE",EDGE,{"disambiguationData":[OSD([sQuery(id+"F7.wireOp",EDGE,"E10")])],"isStart":false});
            transform(context, id + "F52", {"entities" : qUnion([Q0]), "transformType" : TransformType.ROTATION, "transformAxis" : qUnion([Q2]), "angle" : 90 * degree, "makeCopy" : false});
        }
        {
            var Q0;
            Q0=makeQuery(id+"F13.opRevolve","SWEPT_BODY",BODY,{"disambiguationData":[OSD([sQuery(id+"F12.wireOp",EDGE,"E20"),sQuery(id+"F12.wireOp",EDGE,"E24"),sQuery(id+"F12.wireOp",EDGE,"E26"),sQuery(id+"F12.wireOp",EDGE,"E27"),sQuery(id+"F12.wireOp",EDGE,"E28"),sQuery(id+"F12.wireOp",EDGE,"E30")])]});
            var Q1;
            Q1=makeQuery(id+"F14.opExtrude","CAP_EDGE",EDGE,{"disambiguationData":[OSD([sQuery(id+"F12.wireOp",EDGE,"E22")])],"isStart":false});
            transform(context, id + "F53", {"entities" : qUnion([Q0]), "transformType" : TransformType.ROTATION, "transformAxis" : qUnion([Q1]), "angle" : 90 * degree, "makeCopy" : false});
        }
        {
            var Q0;
            Q0=makeQuery(id+"F18.opRevolve","SWEPT_BODY",BODY,{"disambiguationData":[OSD([sQuery(id+"F17.wireOp",EDGE,"E32"),sQuery(id+"F17.wireOp",EDGE,"E36"),sQuery(id+"F17.wireOp",EDGE,"E38"),sQuery(id+"F17.wireOp",EDGE,"E39"),sQuery(id+"F17.wireOp",EDGE,"E40"),sQuery(id+"F17.wireOp",EDGE,"E42")])]});
            var Q1;
            Q1=makeQuery(id+"F19.opExtrude","CAP_EDGE",EDGE,{"disambiguationData":[OSD([sQuery(id+"F17.wireOp",EDGE,"E34")])],"isStart":false});
            transform(context, id + "F54", {"entities" : qUnion([Q0]), "transformType" : TransformType.ROTATION, "transformAxis" : qUnion([Q1]), "angle" : 90 * degree, "makeCopy" : false});
        }
        {
            var Q0;
            Q0=makeQuery(id+"F23.opRevolve","SWEPT_BODY",BODY,{"disambiguationData":[OSD([sQuery(id+"F22.wireOp",EDGE,"E44"),sQuery(id+"F22.wireOp",EDGE,"E48"),sQuery(id+"F22.wireOp",EDGE,"E50"),sQuery(id+"F22.wireOp",EDGE,"E51"),sQuery(id+"F22.wireOp",EDGE,"E52"),sQuery(id+"F22.wireOp",EDGE,"E54")])]});
            var Q1;
            Q1=makeQuery(id+"F24.opExtrude","CAP_EDGE",EDGE,{"disambiguationData":[OSD([sQuery(id+"F22.wireOp",EDGE,"E46")])],"isStart":false});
            transform(context, id + "F55", {"entities" : qUnion([Q0]), "transformType" : TransformType.ROTATION, "transformAxis" : qUnion([Q1]), "angle" : 90 * degree, "makeCopy" : false});
        }
        {
            var Q0;
            Q0=makeQuery(id+"F26.opRevolve","SWEPT_BODY",BODY,{"disambiguationData":[OSD([sQuery(id+"F25.wireOp",EDGE,"E55"),sQuery(id+"F25.wireOp",EDGE,"E59"),sQuery(id+"F25.wireOp",EDGE,"E61"),sQuery(id+"F25.wireOp",EDGE,"E62"),sQuery(id+"F25.wireOp",EDGE,"E63"),sQuery(id+"F25.wireOp",EDGE,"E65")])]});
            var Q1;
            Q1=makeQuery(id+"F27.opExtrude","CAP_EDGE",EDGE,{"disambiguationData":[OSD([sQuery(id+"F25.wireOp",EDGE,"E57")])],"isStart":false});
            transform(context, id + "F56", {"entities" : qUnion([Q0]), "transformType" : TransformType.ROTATION, "transformAxis" : qUnion([Q1]), "angle" : 90 * degree, "makeCopy" : false});
        }
        {
            var Q0;
            Q0=makeQuery(id+"F29.opRevolve","SWEPT_BODY",BODY,{"disambiguationData":[OSD([sQuery(id+"F28.wireOp",EDGE,"E66"),sQuery(id+"F28.wireOp",EDGE,"E70"),sQuery(id+"F28.wireOp",EDGE,"E72"),sQuery(id+"F28.wireOp",EDGE,"E73"),sQuery(id+"F28.wireOp",EDGE,"E74"),sQuery(id+"F28.wireOp",EDGE,"E76")])]});
            var Q1;
            Q1=makeQuery(id+"F30.opExtrude","CAP_EDGE",EDGE,{"disambiguationData":[OSD([sQuery(id+"F28.wireOp",EDGE,"E68")])],"isStart":false});
            transform(context, id + "F57", {"entities" : qUnion([Q0]), "transformType" : TransformType.ROTATION, "transformAxis" : qUnion([Q1]), "angle" : 90 * degree, "makeCopy" : false});
        }
        {
            var Q0;
            Q0=makeQuery(id+"F32.opRevolve","SWEPT_BODY",BODY,{"disambiguationData":[OSD([sQuery(id+"F31.wireOp",EDGE,"E77"),sQuery(id+"F31.wireOp",EDGE,"E81"),sQuery(id+"F31.wireOp",EDGE,"E83"),sQuery(id+"F31.wireOp",EDGE,"E84"),sQuery(id+"F31.wireOp",EDGE,"E85"),sQuery(id+"F31.wireOp",EDGE,"E87")])]});
            var Q1;
            Q1=makeQuery(id+"F33.opExtrude","CAP_EDGE",EDGE,{"disambiguationData":[OSD([sQuery(id+"F31.wireOp",EDGE,"E79")])],"isStart":false});
            transform(context, id + "F58", {"entities" : qUnion([Q0]), "transformType" : TransformType.ROTATION, "transformAxis" : qUnion([Q1]), "angle" : 90 * degree, "makeCopy" : false});
        }
        {
            var Q0;
            Q0=makeQuery(id+"F35.opRevolve","SWEPT_BODY",BODY,{"disambiguationData":[OSD([sQuery(id+"F34.wireOp",EDGE,"E88"),sQuery(id+"F34.wireOp",EDGE,"E92"),sQuery(id+"F34.wireOp",EDGE,"E94"),sQuery(id+"F34.wireOp",EDGE,"E95"),sQuery(id+"F34.wireOp",EDGE,"E96"),sQuery(id+"F34.wireOp",EDGE,"E98")])]});
            var Q1;
            Q1=makeQuery(id+"F36.opExtrude","CAP_EDGE",EDGE,{"disambiguationData":[OSD([sQuery(id+"F34.wireOp",EDGE,"E90")])],"isStart":false});
            transform(context, id + "F59", {"entities" : qUnion([Q0]), "transformType" : TransformType.ROTATION, "transformAxis" : qUnion([Q1]), "angle" : 90 * degree, "makeCopy" : false});
        }
        {
            var Q0;
            Q0=makeQuery(id+"F38.opRevolve","SWEPT_BODY",BODY,{"disambiguationData":[OSD([sQuery(id+"F37.wireOp",EDGE,"E99"),sQuery(id+"F37.wireOp",EDGE,"E103"),sQuery(id+"F37.wireOp",EDGE,"E105"),sQuery(id+"F37.wireOp",EDGE,"E106"),sQuery(id+"F37.wireOp",EDGE,"E107"),sQuery(id+"F37.wireOp",EDGE,"E109")])]});
            var Q1;
            Q1=makeQuery(id+"F39.opExtrude","CAP_EDGE",EDGE,{"disambiguationData":[OSD([sQuery(id+"F37.wireOp",EDGE,"E101")])],"isStart":false});
            transform(context, id + "F60", {"entities" : qUnion([Q0]), "transformType" : TransformType.ROTATION, "transformAxis" : qUnion([Q1]), "angle" : 90 * degree, "makeCopy" : false});
        }
        {
            var Q0;
            Q0=makeQuery(id+"F32.opRevolve","SWEPT_BODY",BODY,{"disambiguationData":[OSD([sQuery(id+"F31.wireOp",EDGE,"E77"),sQuery(id+"F31.wireOp",EDGE,"E81"),sQuery(id+"F31.wireOp",EDGE,"E83"),sQuery(id+"F31.wireOp",EDGE,"E84"),sQuery(id+"F31.wireOp",EDGE,"E85"),sQuery(id+"F31.wireOp",EDGE,"E87")])]});
            transform(context, id + "F61", {"entities" : qUnion([Q0]), "transformType" : TransformType.TRANSLATION_3D, "dx" : 0 * mm, "dy" : 0 * mm, "dz" : 3.5 * mm, "makeCopy" : false});
        }
        {
            var Q0;
            Q0=makeQuery(id+"F2.opExtrude","CAP_FACE",FACE,{"disambiguationData":[OSD([sQuery(id+"F0.wireOp",EDGE,"E0"),sQuery(id+"F0.wireOp",EDGE,"E1"),sQuery(id+"F0.wireOp",EDGE,"E2"),sQuery(id+"F0.wireOp",EDGE,"E3")])],"isStart":false});
            var sketch = newSketch(context, id + "F62", { "sketchPlane" : qUnion([Q0])});
            skLineSegment(sketch, "E116", {"start": v(-48.63, 10) * mm, "end": v(-48.63, 0) * mm, "construction": true});
            skLineSegment(sketch, "E117", {"start": v(-58.63, 5) * mm, "end": v(-38.63, 5) * mm, "construction": true});
            skPoint(sketch, "E118", {"position": v(-48.63, 5) * mm});
            skCircle(sketch, "E119", {"center": v(-48.63, 5) * mm, "radius": 2.5 * mm});
            skSolve(sketch);
        }
        {
            var Q0;
            Q0=makeQuery(id+"F62.imprint","IMPRINT",FACE,{"disambiguationData":[TD([[makeQuery(id+"F62.imprint","IMPRINT",EDGE,{"derivedFrom":sQuery(id+"F62.wireOp",EDGE,"E119")}),1.0]])]});
            extrude(context, id + "F63", {"entities" : qUnion([Q0]), "operationType" : NewBodyOperationType.REMOVE, "oppositeDirection" : true, "depth" : 25 * mm});
        }
        {
            var Q0;
            Q0=makeQuery(id+"F4.opPattern","COPY",BODY,{"derivedFrom":makeQuery(id+"F1.opRevolve","SWEPT_BODY",BODY,{"disambiguationData":[OSD([sQuery(id+"F0.wireOp",EDGE,"E0"),sQuery(id+"F0.wireOp",EDGE,"E4"),sQuery(id+"F0.wireOp",EDGE,"E5"),sQuery(id+"F0.wireOp",EDGE,"E6"),sQuery(id+"F0.wireOp",EDGE,"E7")])]}),"instanceName":"1"});
            var Q1;
            Q1=makeQuery(id+"F6.opPattern","COPY",BODY,{"derivedFrom":makeQuery(id+"F4.opPattern","COPY",BODY,{"derivedFrom":makeQuery(id+"F1.opRevolve","SWEPT_BODY",BODY,{"disambiguationData":[OSD([sQuery(id+"F0.wireOp",EDGE,"E0"),sQuery(id+"F0.wireOp",EDGE,"E4"),sQuery(id+"F0.wireOp",EDGE,"E5"),sQuery(id+"F0.wireOp",EDGE,"E6"),sQuery(id+"F0.wireOp",EDGE,"E7")])]}),"instanceName":"1"}),"instanceName":"1"});
            deleteBodies(context, id + "F64", {"entities" : qUnion([Q0, Q1])});
        }
        {
            var Q0;
            Q0=makeQuery(id+"F1.opRevolve","SWEPT_BODY",BODY,{"disambiguationData":[OSD([sQuery(id+"F0.wireOp",EDGE,"E0"),sQuery(id+"F0.wireOp",EDGE,"E4"),sQuery(id+"F0.wireOp",EDGE,"E5"),sQuery(id+"F0.wireOp",EDGE,"E6"),sQuery(id+"F0.wireOp",EDGE,"E7")])]});
            transform(context, id + "F65", {"entities" : qUnion([Q0]), "transformType" : TransformType.TRANSLATION_3D, "dx" : 0 * mm, "dy" : -46 * mm, "dz" : 0 * mm, "makeCopy" : true});
        }
        {
            var Q0;
            Q0=makeQuery(id+"F65.opPattern","COPY",BODY,{"derivedFrom":makeQuery(id+"F1.opRevolve","SWEPT_BODY",BODY,{"disambiguationData":[OSD([sQuery(id+"F0.wireOp",EDGE,"E0"),sQuery(id+"F0.wireOp",EDGE,"E4"),sQuery(id+"F0.wireOp",EDGE,"E5"),sQuery(id+"F0.wireOp",EDGE,"E6"),sQuery(id+"F0.wireOp",EDGE,"E7")])]}),"instanceName":"1"});
            transform(context, id + "F66", {"entities" : qUnion([Q0]), "transformType" : TransformType.TRANSLATION_3D, "dx" : 0 * mm, "dy" : -41 * mm, "dz" : 0 * mm, "makeCopy" : true});
        }
    });
